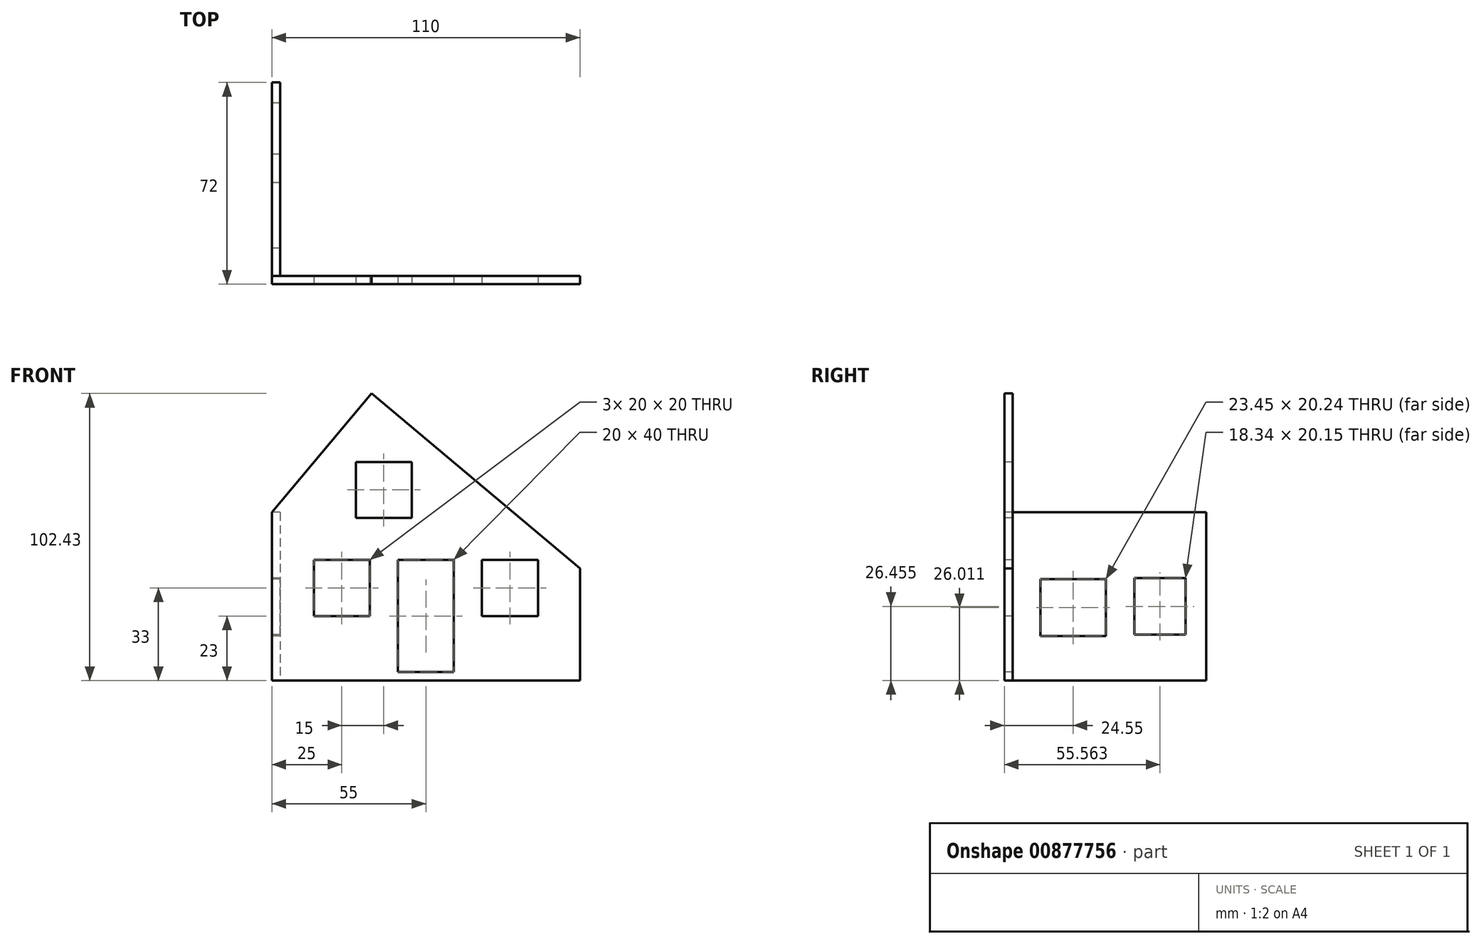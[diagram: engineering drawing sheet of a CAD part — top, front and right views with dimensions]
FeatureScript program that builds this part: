
annotation { "Feature Type Name" : "Feature", "Feature Type Description" : "" }
export const myFeature = defineFeature(function(context is Context, id is Id, definition is map)
    precondition{}
    {
        {
            var Q0;
            Q0=qCreatedBy(makeId("Top.planeOp"),FACE);
            var sketch = newSketch(context, id + "F0", { "sketchPlane" : qUnion([Q0])});
            skLineSegment(sketch, "E0.bottom", {"start": v(-110, 0) * mm, "end": v(0, 0) * mm});
            skLineSegment(sketch, "E0.top", {"start": v(-110, 75) * mm, "end": v(0, 75) * mm});
            skLineSegment(sketch, "E0.left", {"start": v(-110, 0) * mm, "end": v(-110, 75) * mm});
            skLineSegment(sketch, "E0.right", {"start": v(0, 0) * mm, "end": v(0, 75) * mm});
            skLineSegment(sketch, "E1.bottom", {"start": v(-63.22, 63.26) * mm, "end": v(-61.47, 63.26) * mm});
            skLineSegment(sketch, "E1.top", {"start": v(-63.22, 64.28) * mm, "end": v(-61.47, 64.28) * mm});
            skLineSegment(sketch, "E1.left", {"start": v(-63.22, 63.26) * mm, "end": v(-63.22, 64.28) * mm});
            skLineSegment(sketch, "E1.right", {"start": v(-61.47, 63.26) * mm, "end": v(-61.47, 64.28) * mm});
            skLineSegment(sketch, "E2", {"start": v(-110, 3) * mm, "end": v(0, 3) * mm});
            skLineSegment(sketch, "E3", {"start": v(-110, 72) * mm, "end": v(0, 72) * mm});
            skLineSegment(sketch, "E4", {"start": v(-107, 72) * mm, "end": v(-107, 3) * mm});
            skLineSegment(sketch, "E5", {"start": v(-3, 72) * mm, "end": v(-3, 3) * mm});
            skSolve(sketch);
        }
        {
            var Q0;
            Q0=qCreatedBy(makeId("Front.planeOp"),FACE);
            var sketch = newSketch(context, id + "F1", { "sketchPlane" : qUnion([Q0])});
            skLineSegment(sketch, "E6", {"start": v(-110, 0) * mm, "end": v(-110, 60) * mm});
            skLineSegment(sketch, "E7", {"start": v(-110, 60) * mm, "end": v(-74.4, 102.43) * mm});
            skLineSegment(sketch, "E8", {"start": v(-74.4, 102.43) * mm, "end": v(0, 40) * mm});
            skLineSegment(sketch, "E9", {"start": v(0, 40) * mm, "end": v(0, 0) * mm});
            skLineSegment(sketch, "E10", {"start": v(0, 0) * mm, "end": v(-110, 0) * mm});
            skLineSegment(sketch, "E11.bottom", {"start": v(-15, 43) * mm, "end": v(-35, 43) * mm});
            skLineSegment(sketch, "E11.top", {"start": v(-15, 23) * mm, "end": v(-35, 23) * mm});
            skLineSegment(sketch, "E11.left", {"start": v(-15, 43) * mm, "end": v(-15, 23) * mm});
            skLineSegment(sketch, "E11.right", {"start": v(-35, 43) * mm, "end": v(-35, 23) * mm});
            skLineSegment(sketch, "E12.bottom", {"start": v(-45, 3) * mm, "end": v(-65, 3) * mm});
            skLineSegment(sketch, "E12.top", {"start": v(-45, 43) * mm, "end": v(-65, 43) * mm});
            skLineSegment(sketch, "E12.left", {"start": v(-45, 3) * mm, "end": v(-45, 43) * mm});
            skLineSegment(sketch, "E12.right", {"start": v(-65, 3) * mm, "end": v(-65, 43) * mm});
            skLineSegment(sketch, "E13.bottom", {"start": v(-75, 43) * mm, "end": v(-95, 43) * mm});
            skLineSegment(sketch, "E13.top", {"start": v(-75, 23) * mm, "end": v(-95, 23) * mm});
            skLineSegment(sketch, "E13.left", {"start": v(-75, 43) * mm, "end": v(-75, 23) * mm});
            skLineSegment(sketch, "E13.right", {"start": v(-95, 43) * mm, "end": v(-95, 23) * mm});
            skLineSegment(sketch, "E14.bottom", {"start": v(-80, 78) * mm, "end": v(-60, 78) * mm});
            skLineSegment(sketch, "E14.top", {"start": v(-80, 58) * mm, "end": v(-60, 58) * mm});
            skLineSegment(sketch, "E14.left", {"start": v(-80, 78) * mm, "end": v(-80, 58) * mm});
            skLineSegment(sketch, "E14.right", {"start": v(-60, 78) * mm, "end": v(-60, 58) * mm});
            skSolve(sketch);
        }
        {
            var Q0;
            Q0=makeQuery(id+"F1.imprint","IMPRINT",FACE,{"disambiguationData":[TD([[makeQuery(id+"F1.imprint","IMPRINT",EDGE,{"derivedFrom":sQuery(id+"F1.wireOp",EDGE,"E6")}),-1.0]])]});
            var Q1;
            Q1=sQuery(id+"F0.wireOp",VERTEX,"E2.start");
            extrude(context, id + "F2", {"entities" : qUnion([Q0]), "endBound" : BoundingType.UP_TO_VERTEX, "oppositeDirection" : true, "depth" : 25 * mm, "endBoundEntityVertex" : qUnion([Q1]), "offsetDistance" : 25 * mm});
        }
        {
            var Q0;
            Q0=qCreatedBy(makeId("Right.planeOp"),FACE);
            var Q1;
            Q1=sQuery(id+"F0.wireOp",VERTEX,"E0.top.start");
            cPlane(context, id + "F3", {"entities" : qUnion([Q0, Q1]), "cplaneType" : CPlaneType.PLANE_POINT, "offset" : 25 * mm, "width" : 150 * mm, "height" : 150 * mm});
        }
        {
            var Q0;
            Q0=qCreatedBy(id+"F3.planeOp",FACE);
            var sketch = newSketch(context, id + "F4", { "sketchPlane" : qUnion([Q0])});
            skLineSegment(sketch, "E15.bottom", {"start": v(72, 60) * mm, "end": v(3, 60) * mm});
            skLineSegment(sketch, "E15.top", {"start": v(72, 0) * mm, "end": v(3, 0) * mm});
            skLineSegment(sketch, "E15.left", {"start": v(72, 60) * mm, "end": v(72, 0) * mm});
            skLineSegment(sketch, "E15.right", {"start": v(3, 60) * mm, "end": v(3, 0) * mm});
            skLineSegment(sketch, "E16.bottom", {"start": v(36.28, 15.9) * mm, "end": v(12.82, 15.9) * mm});
            skLineSegment(sketch, "E16.top", {"start": v(36.28, 36.13) * mm, "end": v(12.82, 36.13) * mm});
            skLineSegment(sketch, "E16.left", {"start": v(12.82, 36.13) * mm, "end": v(12.82, 15.9) * mm});
            skLineSegment(sketch, "E16.right", {"start": v(36.28, 36.13) * mm, "end": v(36.28, 15.9) * mm});
            skLineSegment(sketch, "E17.bottom", {"start": v(64.74, 36.53) * mm, "end": v(46.4, 36.53) * mm});
            skLineSegment(sketch, "E17.top", {"start": v(64.74, 16.38) * mm, "end": v(46.4, 16.38) * mm});
            skLineSegment(sketch, "E17.left", {"start": v(46.4, 16.38) * mm, "end": v(46.4, 36.53) * mm});
            skLineSegment(sketch, "E17.right", {"start": v(64.74, 16.38) * mm, "end": v(64.74, 36.53) * mm});
            skSolve(sketch);
        }
        {
            var Q0;
            Q0 = qSketchRegion(id + "F4", true);
            var Q1;
            Q1=sQuery(id+"F0.wireOp",VERTEX,"E4.start");
            extrude(context, id + "F5", {"entities" : qUnion([Q0]), "endBound" : BoundingType.UP_TO_VERTEX, "depth" : 25 * mm, "endBoundEntityVertex" : qUnion([Q1]), "offsetDistance" : 25 * mm});
        }
    });
